# Revit family: ERA_LF_WR_LPR-021
name_source: partatom
category: Осветительные приборы
units: mm (PartAtom-declared; Revit-internal decimal feet)

## family parameters
Всегда вертикально = Да
Заголовок OmniClass = Lighting
Источник света = Да
На основе рабочей плоскости = Нет
Номер OmniClass = 23.80.70.00
Общий = Нет
При загрузке вырезать с полостями = Нет
Размер круглого соединителя = Использовать диаметр
Тип детали = Нормальный
Точка расчета площади = Да

## types (16) — shared parameters
ADSK_Единица измерения = шт.
ADSK_Завод-изготовитель = ЭРА
ADSK_Классификация нагрузок = Освещение
ADSK_Количество фаз = 1
ADSK_Коэффициент мощности = 0.9
ADSK_Наименование краткое = Светильник
ADSK_Напряжение = 230 В
ADSK_Примечание = Линейный AC/DC без гальваничесокй развязки
URL = https://www.eraworld.ru
_Корпус_Диаметр = 1 мм
Видимая форма излучения при визуализации = Нет
Геометрия изделия = Прямоугольный
Источник света = LED
Класс защиты = I
Класс пожароопасности = Нет
Комплект = Линейный AC/DC без гальваничесокй развязки
Разработчик модели = https://www.teslabim.ru
Светофильтр = 16777215
Смещение цветовой температуры при затухании лампы = <Нет>
Степень защиты IP = IP65
Тип установки = Настенный
УГО_Масштаб = 100
Угол наклона = 90,00°
Цвет = Чёрный
zero-valued in all types: ADSK_Размер_Диаметр

## per-type parameters (varying)
| type | ADSK_Марка | ADSK_Масса | ADSK_Наименование | ADSK_Номинальная мощность | ADSK_Обозначение | ADSK_Полная мощность | ADSK_Размер_Высота | ADSK_Размер_Длина | ADSK_Размер_Ширина | _Корпус_Высота | _Корпус_Длина | _Корпус_Ширина | _УГО_Диаметр | _УГО_Длина | _УГО_Ширина | Излучение по длине прямоугольника | Излучение по ширине прямоугольника | Файл фотометрической сетки |
| LPR-021-0-30K-010, LED, IP65, 95х62х35 мм (ДхШхВ), 10 Вт, 3000 К, 620 лм, класс защиты I, в комплекте (линейный ac/dc без гальваничесокй развязки) | LPR-021-0-30K-010 | 0.13 | Светильник, LED, прямоугольный, настенный, IP65, 95х62х35 мм (ДхШхВ), 10 Вт, 3000 К, 620 лм, класс защиты I, в комплекте (линейный ac/dc без гальваничесокй развязки) | 10 Вт | LPR-021-0-30K-010 | 11 В·А | 35 мм | 95 мм | 62 мм | 35 мм | 95 мм | 62 мм | 1 мм | 1 мм | 1 мм | 95 мм | 62 мм | LPR-021-0-30K-010.ies |
| LPR-021-0-30K-020, LED, IP65, 125х75х35 мм (ДхШхВ), 20 Вт, 3000 К, 1160 лм, класс защиты I, в комплекте (линейный ac/dc без гальваничесокй развязки) | LPR-021-0-30K-020 | 0.191 | Светильник, LED, прямоугольный, настенный, IP65, 125х75х35 мм (ДхШхВ), 20 Вт, 3000 К, 1160 лм, класс защиты I, в комплекте (линейный ac/dc без гальваничесокй развязки) | 20 Вт | LPR-021-0-30K-020 | 22 В·А | 35 мм | 125 мм | 75 мм | 35 мм | 125 мм | 75 мм | 1.25 мм | 1.25 мм | 1 мм | 125 мм | 75 мм | LPR-021-0-30K-020.ies |
| LPR-021-0-30K-030, LED, IP65, 139х104х35 мм (ДхШхВ), 30 Вт, 3000 К, 2200 лм, класс защиты I, в комплекте (линейный ac/dc без гальваничесокй развязки) | LPR-021-0-30K-030 | 0.273 | Светильник, LED, прямоугольный, настенный, IP65, 139х104х35 мм (ДхШхВ), 30 Вт, 3000 К, 2200 лм, класс защиты I, в комплекте (линейный ac/dc без гальваничесокй развязки) | 30 Вт | LPR-021-0-30K-030 | 33 В·А | 35 мм | 139 мм | 104 мм | 35 мм | 139 мм | 104 мм | 1.39 мм | 1.39 мм | 1.04 мм | 139 мм | 104 мм | LPR-021-0-30K-030.ies |
| LPR-021-0-30K-050, LED, IP65, 183х131х36 мм (ДхШхВ), 50 Вт, 3000 К, 3200 лм, класс защиты I, в комплекте (линейный ac/dc без гальваничесокй развязки) | LPR-021-0-30K-050 | 0.435 | Светильник, LED, прямоугольный, настенный, IP65, 183х131х36 мм (ДхШхВ), 50 Вт, 3000 К, 3200 лм, класс защиты I, в комплекте (линейный ac/dc без гальваничесокй развязки) | 50 Вт | LPR-021-0-30K-050 | 56 В·А | 36 мм | 183 мм | 131 мм | 36 мм | 183 мм | 131 мм | 1.83 мм | 1.83 мм | 1.31 мм | 183 мм | 131 мм | LPR-021-0-30K-050.ies |
| LPR-021-0-40K-010, LED, IP65, 95х62х35 мм (ДхШхВ), 10 Вт, 4000 К, 620 лм, класс защиты I, в комплекте (линейный ac/dc без гальваничесокй развязки) | LPR-021-0-40K-010 | 0.13 | Светильник, LED, прямоугольный, настенный, IP65, 95х62х35 мм (ДхШхВ), 10 Вт, 4000 К, 620 лм, класс защиты I, в комплекте (линейный ac/dc без гальваничесокй развязки) | 10 Вт | LPR-021-0-40K-010 | 11 В·А | 35 мм | 95 мм | 62 мм | 35 мм | 95 мм | 62 мм | 1 мм | 1 мм | 1 мм | 95 мм | 62 мм | LPR-021-0-40K-010.ies |
| LPR-021-0-40K-020, LED, IP65, 125х75х35 мм (ДхШхВ), 20 Вт, 4000 К, 1160 лм, класс защиты I, в комплекте (линейный ac/dc без гальваничесокй развязки) | LPR-021-0-40K-020 | 0.191 | Светильник, LED, прямоугольный, настенный, IP65, 125х75х35 мм (ДхШхВ), 20 Вт, 4000 К, 1160 лм, класс защиты I, в комплекте (линейный ac/dc без гальваничесокй развязки) | 20 Вт | LPR-021-0-40K-020 | 22 В·А | 35 мм | 125 мм | 75 мм | 35 мм | 125 мм | 75 мм | 1.25 мм | 1.25 мм | 1 мм | 125 мм | 75 мм | LPR-021-0-40K-020.ies |
| LPR-021-0-40K-030, LED, IP65, 139х104х35 мм (ДхШхВ), 30 Вт, 4000 К, 2200 лм, класс защиты I, в комплекте (линейный ac/dc без гальваничесокй развязки) | LPR-021-0-40K-030 | 0.273 | Светильник, LED, прямоугольный, настенный, IP65, 139х104х35 мм (ДхШхВ), 30 Вт, 4000 К, 2200 лм, класс защиты I, в комплекте (линейный ac/dc без гальваничесокй развязки) | 30 Вт | LPR-021-0-40K-030 | 33 В·А | 35 мм | 139 мм | 104 мм | 35 мм | 139 мм | 104 мм | 1.39 мм | 1.39 мм | 1.04 мм | 139 мм | 104 мм | LPR-021-0-40K-030.ies |
| LPR-021-0-40K-050, LED, IP65, 183х131х36 мм (ДхШхВ), 50 Вт, 4000 К, 3200 лм, класс защиты I, в комплекте (линейный ac/dc без гальваничесокй развязки) | LPR-021-0-40K-050 | 0.435 | Светильник, LED, прямоугольный, настенный, IP65, 183х131х36 мм (ДхШхВ), 50 Вт, 4000 К, 3200 лм, класс защиты I, в комплекте (линейный ac/dc без гальваничесокй развязки) | 50 Вт | LPR-021-0-40K-050 | 56 В·А | 36 мм | 183 мм | 131 мм | 36 мм | 183 мм | 131 мм | 1.83 мм | 1.83 мм | 1.31 мм | 183 мм | 131 мм | LPR-021-0-40K-050.ies |
| LPR-021-0-65K-010, LED, IP65, 95х62х35 мм (ДхШхВ), 10 Вт, 6500 К, 620 лм, класс защиты I, в комплекте (линейный ac/dc без гальваничесокй развязки) | LPR-021-0-65K-010 | 0.13 | Светильник, LED, прямоугольный, настенный, IP65, 95х62х35 мм (ДхШхВ), 10 Вт, 6500 К, 620 лм, класс защиты I, в комплекте (линейный ac/dc без гальваничесокй развязки) | 10 Вт | LPR-021-0-65K-010 | 11 В·А | 35 мм | 95 мм | 62 мм | 35 мм | 95 мм | 62 мм | 1 мм | 1 мм | 1 мм | 95 мм | 62 мм | LPR-021-0-65K-010.ies |
| LPR-021-0-65K-020, LED, IP65, 125х75х35 мм (ДхШхВ), 20 Вт, 6500 К, 1160 лм, класс защиты I, в комплекте (линейный ac/dc без гальваничесокй развязки) | LPR-021-0-65K-020 | 0.191 | Светильник, LED, прямоугольный, настенный, IP65, 125х75х35 мм (ДхШхВ), 20 Вт, 6500 К, 1160 лм, класс защиты I, в комплекте (линейный ac/dc без гальваничесокй развязки) | 20 Вт | LPR-021-0-65K-020 | 22 В·А | 35 мм | 125 мм | 75 мм | 35 мм | 125 мм | 75 мм | 1.25 мм | 1.25 мм | 1 мм | 125 мм | 75 мм | LPR-021-0-65K-020.ies |
| LPR-021-0-65K-030, LED, IP65, 139х104х35 мм (ДхШхВ), 30 Вт, 6500 К, 2200 лм, класс защиты I, в комплекте (линейный ac/dc без гальваничесокй развязки) | LPR-021-0-65K-030 | 0.273 | Светильник, LED, прямоугольный, настенный, IP65, 139х104х35 мм (ДхШхВ), 30 Вт, 6500 К, 2200 лм, класс защиты I, в комплекте (линейный ac/dc без гальваничесокй развязки) | 30 Вт | LPR-021-0-65K-030 | 33 В·А | 35 мм | 139 мм | 104 мм | 35 мм | 139 мм | 104 мм | 1.39 мм | 1.39 мм | 1.04 мм | 139 мм | 104 мм | LPR-021-0-65K-030.ies |
| LPR-021-0-65K-050, LED, IP65, 183х131х36 мм (ДхШхВ), 50 Вт, 6500 К, 3200 лм, класс защиты I, в комплекте (линейный ac/dc без гальваничесокй развязки) | LPR-021-0-65K-050 | 0.435 | Светильник, LED, прямоугольный, настенный, IP65, 183х131х36 мм (ДхШхВ), 50 Вт, 6500 К, 3200 лм, класс защиты I, в комплекте (линейный ac/dc без гальваничесокй развязки) | 50 Вт | LPR-021-0-65K-050 | 56 В·А | 36 мм | 183 мм | 131 мм | 36 мм | 183 мм | 131 мм | 1.83 мм | 1.83 мм | 1.31 мм | 183 мм | 131 мм | LPR-021-0-65K-050.ies |
| LPR-021-0-65K-070, LED, IP65, 217х165х36 мм (ДхШхВ), 70 Вт, 6500 К, 5300 лм, класс защиты I, в комплекте (линейный ac/dc без гальваничесокй развязки) | LPR-021-0-65K-070 | 0.645 | Светильник, LED, прямоугольный, настенный, IP65, 217х165х36 мм (ДхШхВ), 70 Вт, 6500 К, 5300 лм, класс защиты I, в комплекте (линейный ac/dc без гальваничесокй развязки) | 70 Вт | LPR-021-0-65K-070 | 78 В·А | 36 мм | 217 мм | 165 мм | 36 мм | 217 мм | 165 мм | 2.17 мм | 2.17 мм | 1.65 мм | 217 мм | 165 мм | LPR-021-0-65K-070.ies |
| LPR-021-0-65K-100, LED, IP65, 251х183х36 мм (ДхШхВ), 100 Вт, 6500 К, 6100 лм, класс защиты I, в комплекте (линейный ac/dc без гальваничесокй развязки) | LPR-021-0-65K-100 | 0.84 | Светильник, LED, прямоугольный, настенный, IP65, 251х183х36 мм (ДхШхВ), 100 Вт, 6500 К, 6100 лм, класс защиты I, в комплекте (линейный ac/dc без гальваничесокй развязки) | 100 Вт | LPR-021-0-65K-100 | 111 В·А | 36 мм | 251 мм | 183 мм | 36 мм | 251 мм | 183 мм | 2.51 мм | 2.51 мм | 1.83 мм | 251 мм | 183 мм | LPR-021-0-65K-100.ies |
| LPR-021-0-65K-150, LED, IP65, 330х270х47 мм (ДхШхВ), 150 Вт, 6500 К, 14800 лм, класс защиты I, в комплекте (линейный ac/dc без гальваничесокй развязки) | LPR-021-0-65K-150 | 1.983 | Светильник, LED, прямоугольный, настенный, IP65, 330х270х47 мм (ДхШхВ), 150 Вт, 6500 К, 14800 лм, класс защиты I, в комплекте (линейный ac/dc без гальваничесокй развязки) | 150 Вт | LPR-021-0-65K-150 | 167 В·А | 47 мм | 330 мм | 270 мм | 47 мм | 330 мм | 270 мм | 3.3 мм | 3.3 мм | 2.7 мм | 330 мм | 270 мм | LPR-021-0-65K-150.ies |
| LPR-021-0-65K-200, LED, IP65, 390х330х50 мм (ДхШхВ), 200 Вт, 6500 К, 18800 лм, класс защиты I, в комплекте (линейный ac/dc без гальваничесокй развязки) | LPR-021-0-65K-200 | 3.48 | Светильник, LED, прямоугольный, настенный, IP65, 390х330х50 мм (ДхШхВ), 200 Вт, 6500 К, 18800 лм, класс защиты I, в комплекте (линейный ac/dc без гальваничесокй развязки) | 200 Вт | LPR-021-0-65K-200 | 222 В·А | 50 мм | 390 мм | 330 мм | 50 мм | 390 мм | 330 мм | 3.9 мм | 3.9 мм | 3.3 мм | 390 мм | 330 мм | LPR-021-0-65K-200.ies |
